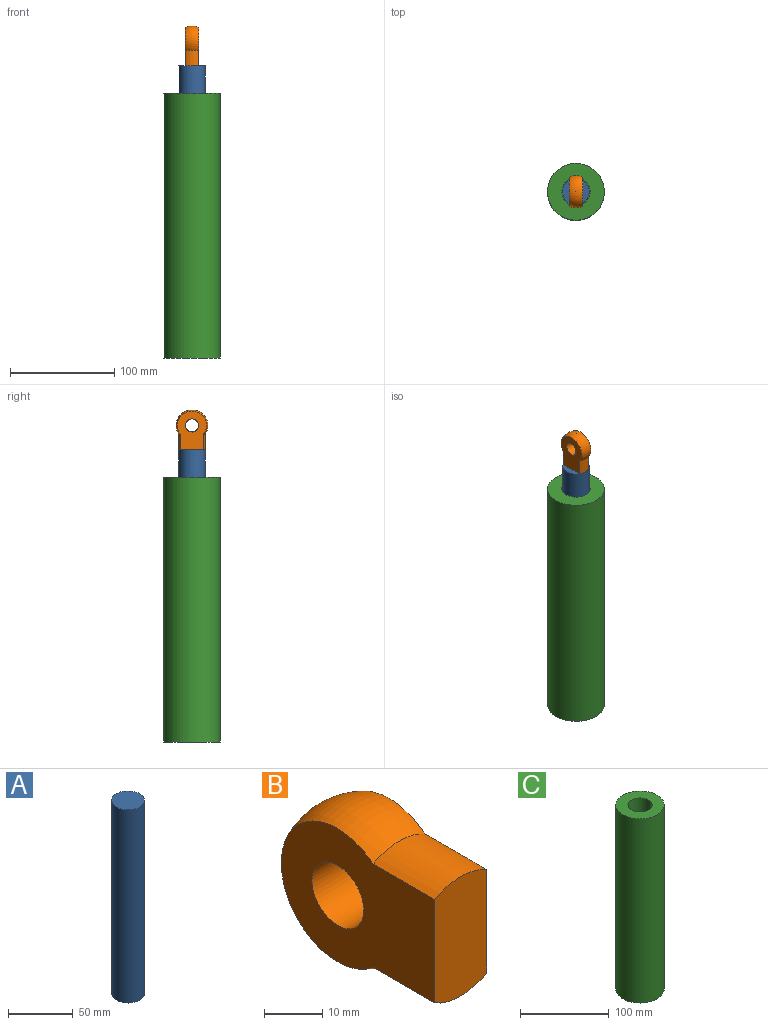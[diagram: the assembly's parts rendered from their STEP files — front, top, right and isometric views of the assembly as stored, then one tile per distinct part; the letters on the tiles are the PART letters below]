
ASSEMBLY  parts=3 mates=4
PART A: 3 faces, bbox 25.4x25.4x183.2 mm
  f0: plane 25.41x25.41mm, normal (0,0,-1), area 507mm2, adj f2
  f1: plane 25.41x25.41mm, normal (0,0,1), area 507mm2, adj f2
  f2: cylinder r=12.7mm len=183.15mm, axis (0,0,1), area 14619.5mm2, adj f0,f1
PART B: 7 faces, bbox 30.7x39x29.5 mm
  f0: cylinder r=12.56mm len=14.95mm, axis (0,1,0), area 197.4mm2, adj f1,f3,f4,f5
  f1: plane 25.11x12.6mm, normal (0,-1,0), area 302.7mm2, adj f0,f2,f4,f5
  f2: cylinder r=12.56mm len=14.95mm, axis (0,1,0), area 197.4mm2, adj f1,f3,f4,f5
  f3: torus R=0.59mm, axis (0,1,0), area 840.5mm2, adj f0,f2,f4,f5
  f4: plane 37.22x28.02mm, normal (-1,0,0), area 726mm2, adj f0,f1,f2,f3,f6
  f5: plane 37.23x28.02mm, normal (1,0,0), area 726.5mm2, adj f0,f1,f2,f3,f6
  f6: cylinder r=6.29mm len=12.6mm, axis (1,0,0), area 498.1mm2, adj f4,f5
PART C: 5 faces, bbox 54.5x54.5x254 mm
  f0: cylinder r=13.59mm len=177.8mm, axis (0,0,1), area 15181.7mm2, adj f2,f4
  f1: cylinder r=27.23mm len=254mm, axis (0,0,1), area 43462.5mm2, adj f2,f3
  f2: plane 54.47x54.47mm, normal (0,0,1), area 1749.8mm2, adj f0,f1
  f3: plane 54.47x54.47mm, normal (0,0,-1), area 2330mm2, adj f1
  f4: plane 27.18x27.18mm, normal (0,0,1), area 580.2mm2, adj f0
PLACE A t=(-119.73,137.08,60.17)mm
PLACE B rot(axis=(1,0,0),90deg) t=(-145.48,137.08,243.32)mm
PLACE C t=(-145.48,137.08,-37.06)mm
MATE cylindrical A.f2 <-> C.f0  axis (0,0,1) through (-145.48,137.08,151.75)mm
MATE fastened B.f0 <-> A.f2  axis (0,0,-1) through (-145.48,137.08,243.32)mm
MATE parallel B.f0 <-> A.f2  axis (0,0,-1) through (-145.48,137.08,243.32)mm
MATE planar B.f0 <-> A.f2  axis (0,0,-1) through (-145.48,137.08,243.32)mm
